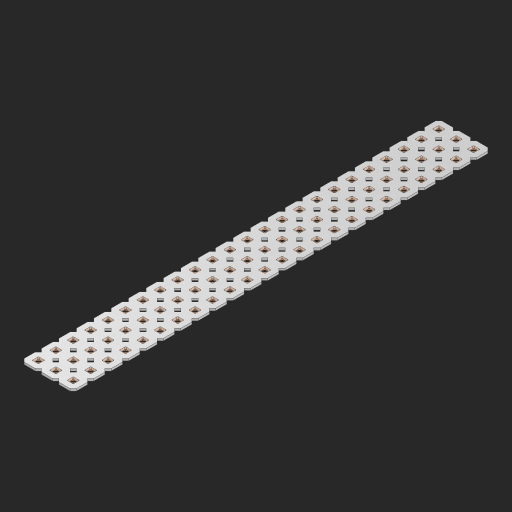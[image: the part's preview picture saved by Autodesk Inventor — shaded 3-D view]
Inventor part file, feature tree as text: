
AUTODESK INVENTOR PART (.ipt)
format: ipt  version: 2023 (Build 270158000, 158)  size: 1,108,480 bytes
history: native  units: in
note: dims shown in document units (in); Inventor stores cm internally (conversion verified against a paired STEP export)
features: other x73, extrude x71, sketch x2, pattern_linear x1
ambient origin geometry x8: Origin, YZ Plane, XZ Plane, XY Plane, X Axis, Y Axis, Z Axis, Center Point
bodies: Solid1 (feature_tree), Body (feature_tree)
feature tree (147):
  pattern_linear  "Rectangular Pattern1"  Spacing1=0.09in  [1 undecoded]
  sketch  "Sketch1"  dims[d1=0.5in]
  sketch  "Sketch2"  dims[d2=0.182in d3=0.09in d4=0.09in d5=0.09in d6=0.09in d7=0.09in d8=0.09in d9=0.09in d10=0.09in d11=0.02in d13=0.0in d14=0.172in d15=0.0625in d16=0.0in d19=0.5in d22=0.5in]
  other  "Srf1"
  other  "Srf126"
  other  "Srf127"
  other  "Srf128"
  other  "Srf129"
  other  "Srf130"
  other  "Srf131"
  other  "Srf250"
  other  "Srf251"
  other  "Srf252"
  other  "Srf253"
  other  "Srf254"
  other  "Srf255"
  other  "Srf256"
  other  "Srf257"
  other  "Srf258"
  other  "Srf259"
  other  "Srf260"
  other  "Srf261"
  other  "Srf262"
  other  "Srf263"
  other  "Srf264"
  other  "Srf265"
  other  "Srf266"
  other  "Srf268"
  other  "Srf269"
  other  "Srf270"
  other  "Srf271"
  other  "Srf272"
  other  "Srf273"
  other  "Srf274"
  other  "Srf275"
  other  "Srf276"
  other  "Srf277"
  other  "Srf278"
  other  "Srf279"
  other  "Srf280"
  other  "Srf281"
  other  "Srf282"
  other  "Srf283"
  other  "Srf284"
  other  "Srf285"
  other  "Srf286"
  other  "Srf287"
  other  "Srf288"
  other  "Srf289"
  other  "Srf290"
  other  "Srf291"
  other  "Srf293"
  other  "Srf294"
  other  "Srf295"
  other  "Srf296"
  other  "Srf297"
  other  "Srf298"
  other  "Srf299"
  other  "Srf300"
  other  "Srf301"
  other  "Srf302"
  other  "Srf303"
  other  "Srf304"
  other  "Srf305"
  other  "Srf306"
  other  "Srf307"
  other  "Srf308"
  other  "Srf309"
  other  "Srf310"
  other  "Srf311"
  other  "Srf312"
  other  "Srf313"
  other  "Srf314"
  other  "Srf315"
  other  "Srf316"
  other  "Circle"
  extrude  "ExtrusionSrf126"  Depth=0.09in
  extrude  "ExtrusionSrf127"  Depth=0.09in
  extrude  "ExtrusionSrf128"  Depth=0.09in
  extrude  "ExtrusionSrf129"  Depth=0.09in
  extrude  "ExtrusionSrf130"  Depth=0.09in
  extrude  "ExtrusionSrf131"  Depth=0.09in
  extrude  "ExtrusionSrf250"  Depth=0.09in
  extrude  "ExtrusionSrf251"  Depth=0.02in
  extrude  "ExtrusionSrf252"  TaperAngle=0.0deg  [1 undecoded]
  extrude  "ExtrusionSrf253"  Depth=0.5in
  extrude  "ExtrusionSrf254"  Depth=0.0625in TaperAngle=0.0deg
  extrude  "ExtrusionSrf255"  Depth=0.5in
  extrude  "ExtrusionSrf256"  Depth=0.5in
  extrude  "ExtrusionSrf257"  [1 undecoded]
  extrude  "ExtrusionSrf258"  [1 undecoded]
  extrude  "ExtrusionSrf259"  [1 undecoded]
  extrude  "ExtrusionSrf260"  [1 undecoded]
  extrude  "ExtrusionSrf261"  [1 undecoded]
  extrude  "ExtrusionSrf262"  [1 undecoded]
  extrude  "ExtrusionSrf263"  [1 undecoded]
  extrude  "ExtrusionSrf264"  [1 undecoded]
  extrude  "ExtrusionSrf265"  [1 undecoded]
  extrude  "ExtrusionSrf266"  [1 undecoded]
  extrude  "ExtrusionSrf268"  [1 undecoded]
  extrude  "ExtrusionSrf269"  [1 undecoded]
  extrude  "ExtrusionSrf270"  [1 undecoded]
  extrude  "ExtrusionSrf271"  [1 undecoded]
  extrude  "ExtrusionSrf272"  [1 undecoded]
  extrude  "ExtrusionSrf273"  [1 undecoded]
  extrude  "ExtrusionSrf274"  [1 undecoded]
  extrude  "ExtrusionSrf275"  [1 undecoded]
  extrude  "ExtrusionSrf276"  [1 undecoded]
  extrude  "ExtrusionSrf277"  [1 undecoded]
  extrude  "ExtrusionSrf278"  [1 undecoded]
  extrude  "ExtrusionSrf279"  [1 undecoded]
  extrude  "ExtrusionSrf280"  [1 undecoded]
  extrude  "ExtrusionSrf281"  [1 undecoded]
  extrude  "ExtrusionSrf282"  [1 undecoded]
  extrude  "ExtrusionSrf283"  [1 undecoded]
  extrude  "ExtrusionSrf284"  [1 undecoded]
  extrude  "ExtrusionSrf285"  [1 undecoded]
  extrude  "ExtrusionSrf286"  [1 undecoded]
  extrude  "ExtrusionSrf287"  [1 undecoded]
  extrude  "ExtrusionSrf288"  [1 undecoded]
  extrude  "ExtrusionSrf289"  [1 undecoded]
  extrude  "ExtrusionSrf290"  [1 undecoded]
  extrude  "ExtrusionSrf291"  [1 undecoded]
  extrude  "ExtrusionSrf293"  [1 undecoded]
  extrude  "ExtrusionSrf294"  [1 undecoded]
  extrude  "ExtrusionSrf295"  [1 undecoded]
  extrude  "ExtrusionSrf296"  [1 undecoded]
  extrude  "ExtrusionSrf297"  [1 undecoded]
  extrude  "ExtrusionSrf298"  [1 undecoded]
  extrude  "ExtrusionSrf299"  [1 undecoded]
  extrude  "ExtrusionSrf300"  [1 undecoded]
  extrude  "ExtrusionSrf301"  [1 undecoded]
  extrude  "ExtrusionSrf302"  [1 undecoded]
  extrude  "ExtrusionSrf303"  [1 undecoded]
  extrude  "ExtrusionSrf304"  [1 undecoded]
  extrude  "ExtrusionSrf305"  [1 undecoded]
  extrude  "ExtrusionSrf306"  [1 undecoded]
  extrude  "ExtrusionSrf307"  [1 undecoded]
  extrude  "ExtrusionSrf308"  [1 undecoded]
  extrude  "ExtrusionSrf309"  [1 undecoded]
  extrude  "ExtrusionSrf310"  [1 undecoded]
  extrude  "ExtrusionSrf311"  [1 undecoded]
  extrude  "ExtrusionSrf312"  [1 undecoded]
  extrude  "ExtrusionSrf313"  [1 undecoded]
  extrude  "ExtrusionSrf314"  [1 undecoded]
  extrude  "ExtrusionSrf315"  [1 undecoded]
  extrude  "ExtrusionSrf316"  [1 undecoded]
note: 60 required parameter values undecoded (feature->parameter linkage not recoverable at this tier; creation-order binding heuristic only, values carry confidence <= 0.55)
